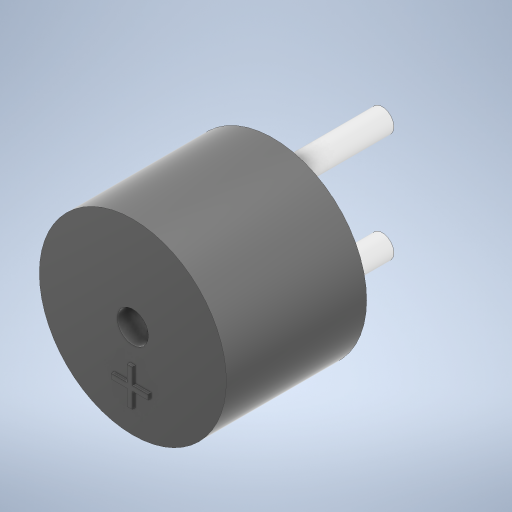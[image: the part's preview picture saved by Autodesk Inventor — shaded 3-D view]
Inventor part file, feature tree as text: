
AUTODESK INVENTOR PART (.ipt)
format: ipt  version: 2024.3 (Build 283343000, 343)  size: 270,336 bytes
history: native  units: mm
features: extrude x4, sketch x3
ambient origin geometry x8: Origin, YZ Plane, XZ Plane, XY Plane, X Axis, Y Axis, Z Axis, Center Point
bodies: Solid1 (feature_tree)
feature tree (7):
  extrude  "Extrusion1"  Depth=9.0mm TaperAngle=0.0deg
  sketch  "Sketch2"  dims[d3=2.0mm d4=5.0mm d5=0.0mm]
  extrude  "Extrusion2"  Depth=5.0mm TaperAngle=0.0deg
  extrude  "Extrusion3"  Depth=7.0mm
  extrude  "Extrusion4"  Depth=7.0mm
  sketch  "Sketch1"  dims[d0=12.0mm d1=9.0mm d2=0.0mm]
  sketch  "Sketch3"  dims[d6=0.2mm d7=0.0mm d8=1.5mm d9=7.0mm d10=7.0mm d11=0.0mm]
